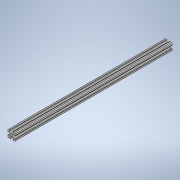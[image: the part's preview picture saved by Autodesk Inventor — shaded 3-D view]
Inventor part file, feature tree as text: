
AUTODESK INVENTOR PART (.ipt)
format: ipt  version: 2020 (Build 240168000, 168)  size: 237,568 bytes
history: native  units: in
note: dims shown in document units (in); Inventor stores cm internally (conversion verified against a paired STEP export)
features: extrude x1, sketch x1
ambient origin geometry x8: Origin, YZ Plane, XZ Plane, XY Plane, X Axis, Y Axis, Z Axis, Center Point
bodies: Solid1 (feature_tree)
feature tree (2):
  extrude  "Extrusion1"  [1 undecoded]
  sketch  "Sketch1"  dims[d0=21.0in d1=0.0in]
note: 1 required parameter value undecoded (feature->parameter linkage not recoverable at this tier; creation-order binding heuristic only, values carry confidence <= 0.55)
